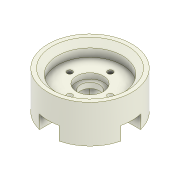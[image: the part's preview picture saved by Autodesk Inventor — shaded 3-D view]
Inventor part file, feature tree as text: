
AUTODESK INVENTOR PART (.ipt)
format: ipt  version: 2022 (Build 260153000, 153)  size: 451,072 bytes
history: native  units: mm
features: sketch x15, extrude x7, hole x7, projected_geometry x5, chamfer x2, plane x2, mirror x1, thicken_offset x1, fillet x1, split x1, boolean_combine x1
ambient origin geometry x8: Origin, YZ Plane, XZ Plane, XY Plane, X Axis, Y Axis, Z Axis, Center Point
bodies: Solid1 (feature_tree), Solid2 (feature_tree), Solid3 (feature_tree)
feature tree (43):
  extrude  "Extrusion1"  Depth=5.0mm TaperAngle=0.0deg
  extrude  "Extrusion2"  Depth=40.0mm TaperAngle=0.0deg
  sketch  "Sketch4"  dims[d9=6.0mm d10=4.0mm d11=2.0mm d12=90.0deg d13=6.0mm d14=0.0mm d15=24.0mm]
  hole  "Hole1"  [1 undecoded]
  mirror  "Mirror1"
  hole  "Hole5"  [1 undecoded]
  thicken_offset  "Thicken1"
  extrude  "Extrusion3"  Depth=5.0mm
  extrude  "Extrusion4"  Depth=4.0mm TaperAngle=45.0deg
  fillet  "Fillet1"  Radius=0.15mm
  hole  "Hole2"  [1 undecoded]
  hole  "Hole3"  [1 undecoded]
  chamfer  "Chamfer1"  Distance=5.0mm
  chamfer  "Chamfer2"  Distance=10.0mm
  plane  "Work Plane1"
  split  "Split1"
  extrude  "Extrusion5"  Depth=10.0mm
  boolean_combine  "Combine1"
  sketch  "Sketch12"  dims[d51=0.15mm]
  plane  "Work Plane2"
  extrude  "Extrusion6"  TaperAngle=0.0deg  [1 undecoded]
  hole  "Hole6"  [1 undecoded]
  hole  "Hole7"  [1 undecoded]
  hole  "Hole8"  [1 undecoded]
  extrude  "Extrusion7"  Depth=10.0mm
  sketch  "Sketch1"  dims[d1=5.0mm d2=24.25mm d3=0.0mm]
  sketch  "Sketch2"  dims[d5=3.0mm d6=40.0mm d7=0.0mm]
  sketch  "Sketch3"  dims[d8=13.0mm]
  sketch  "Sketch5"  dims[d16=5.0mm d17=0.0mm d18=0.0mm d19=0.0mm]
  sketch  "Sketch6"  dims[d20=5.0mm d21=15.0mm]
  sketch  "Sketch7"  dims[d22=40.0mm d24=360.0deg]
  sketch  "Sketch9"  dims[d26=2.0mm d27=6.0mm d28=4.0mm d29=2.0mm d30=90.0deg d31=5.0mm d32=20.594885mm]
  sketch  "Sketch10"  dims[d33=10.0mm d34=6.0mm d35=4.0mm d36=2.0mm d37=90.0deg d38=2.0mm d39=0.0mm d40=2.0mm d41=2.0mm d42=45.0deg d50=0.15mm]
  sketch  "Sketch13"  dims[d52=7.0mm d53=6.0mm d54=4.0mm d55=2.0mm d56=90.0deg d57=6.0mm d58=0.0mm d59=0.5mm d60=2.0mm d61=45.0deg]
  projected_geometry  "Projected Loop1"
  sketch  "Sketch14"  dims[d62=-7.0mm d63=7.0mm]
  sketch  "Sketch15"  dims[d64=7.0mm d65=5.0mm d66=0.0mm]
  sketch  "Sketch16"  dims[d67=14.75mm]
  sketch  "Sketch17"  dims[d68=-14.75mm d69=10.0mm d70=10.0mm d71=0.0mm d72=0.0mm d73=3.4mm d74=6.0mm d75=4.0mm d76=2.0mm d77=90.0deg d78=8.0mm d79=0.0mm d80=3.0mm d81=6.0mm d82=4.0mm d83=2.0mm d84=90.0deg d85=3.0mm d86=0.0mm d87=7.0mm d88=6.0mm d89=4.0mm d90=2.0mm d91=90.0deg d92=3.0mm d93=0.0mm d94=0.15mm d95=10.0mm d96=0.0mm d43=0.15mm d44=0.25mm d45=0.375mm d46=14.3117mm d47=0.75mm d48=20.594885mm d49=0.0625mm]
  projected_geometry  "Project Cut Edges1"
  projected_geometry  "Project Cut Edges2"
  projected_geometry  "Project Cut Edges3"
  projected_geometry  "Project Cut Edges4"
note: 8 required parameter values undecoded (feature->parameter linkage not recoverable at this tier; creation-order binding heuristic only, values carry confidence <= 0.55)
